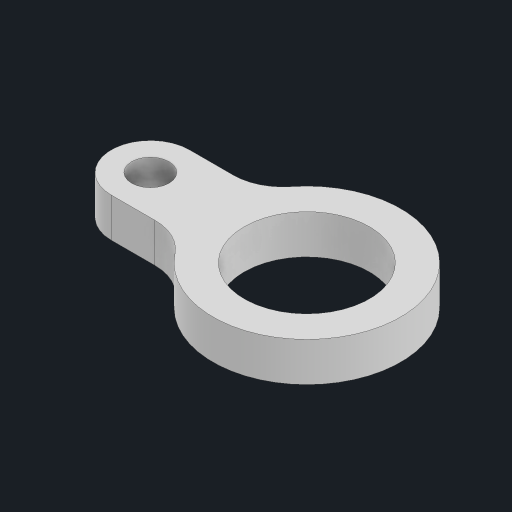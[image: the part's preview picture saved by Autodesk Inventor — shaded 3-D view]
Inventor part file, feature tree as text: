
AUTODESK INVENTOR PART (.ipt)
format: ipt  version: 2023.1 (Build 271208000, 208)  size: 118,272 bytes
history: native  units: mm
features: extrude x1, fillet x1, sketch x1
ambient origin geometry x8: Origin, YZ Plane, XZ Plane, XY Plane, X Axis, Y Axis, Z Axis, Center Point
bodies: Solid1 (feature_tree)
feature tree (3):
  extrude  "Extrusion1"  Depth=20.0mm
  fillet  "Fillet1"  Radius=24.0mm
  sketch  "Sketch1"  dims[d0=16.0mm d1=20.0mm d2=24.0mm d4=10.0mm d5=6.35mm d6=2.25mm d8=5.0mm d9=0.0mm d10=6.35mm]
